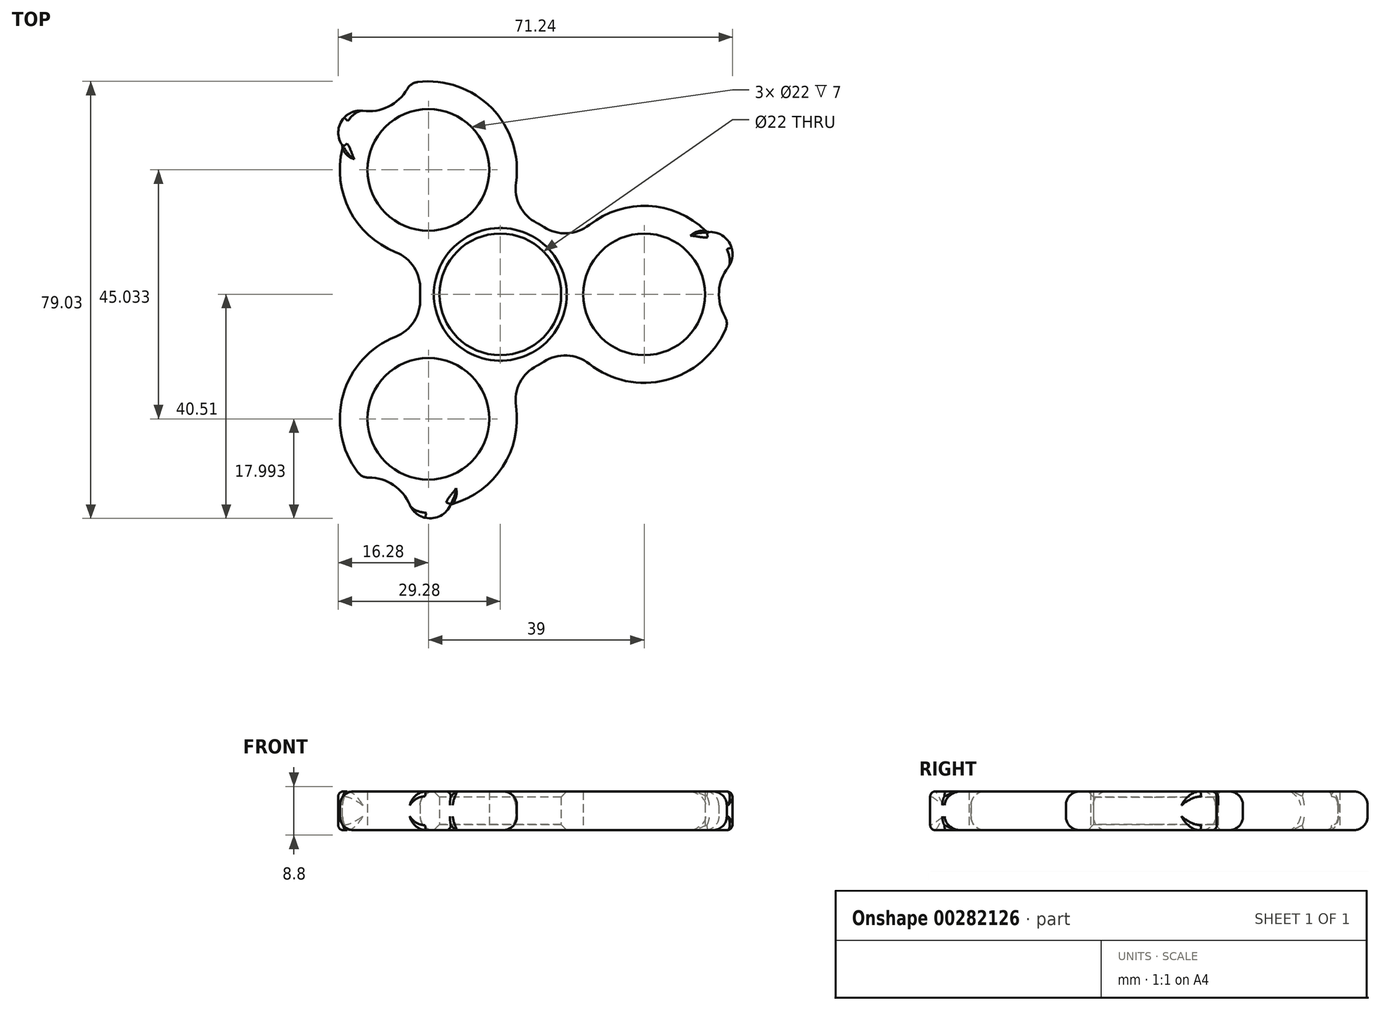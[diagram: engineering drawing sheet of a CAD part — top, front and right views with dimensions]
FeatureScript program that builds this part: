
annotation { "Feature Type Name" : "Feature", "Feature Type Description" : "" }
export const myFeature = defineFeature(function(context is Context, id is Id, definition is map)
    precondition{}
    {
        {
            var Q0;
            Q0=qCreatedBy(makeId("Top.planeOp"),FACE);
            var sketch = newSketch(context, id + "F0", { "sketchPlane" : qUnion([Q0])});
            skCircle(sketch, "E0", {"center": v(0, 0) * mm, "radius": 11 * mm});
            skCircle(sketch, "E1", {"center": v(0, 0) * mm, "radius": 14.5 * mm});
            skLineSegment(sketch, "E2", {"start": v(0, 0) * mm, "end": v(22, 0) * mm, "construction": true});
            skLineSegment(sketch, "E3", {"start": v(0, 0) * mm, "end": v(26, 0) * mm, "construction": true});
            skCircle(sketch, "E4", {"center": v(26, 0) * mm, "radius": 11 * mm});
            skCircle(sketch, "E5", {"center": v(26, 0) * mm, "radius": 16 * mm});
            skArc(sketch, "E6", {"start": v(17.92, 14.74) * mm, "mid": v(11.38, 11.05) * mm, "end": v(5.2, 15.34) * mm});
            skArc(sketch, "E7.MirrorCS", {"start": v(17.92, -14.74) * mm, "mid": v(11.38, -11.05) * mm, "end": v(5.2, -15.34) * mm});
            skLineSegment(sketch, "E8", {"start": v(39.86, 7.99) * mm, "end": v(62.74, 7.99) * mm, "construction": true});
            skLineSegment(sketch, "E9", {"start": v(39.86, -7.99) * mm, "end": v(63.47, -7.99) * mm, "construction": true});
            skArc(sketch, "E10", {"start": v(47.98, 7.99) * mm, "mid": v(39.5, 0) * mm, "end": v(47.98, -7.99) * mm});
            skLineSegment(sketch, "E11", {"start": v(47.5, 0) * mm, "end": v(61.75, 0) * mm, "construction": true});
            skArc(sketch, "E12", {"start": v(41.22, 4.95) * mm, "mid": v(41.38, 9.36) * mm, "end": v(37.4, 11.24) * mm});
            skArc(sketch, "E13.MirrorCS", {"start": v(41.22, -4.95) * mm, "mid": v(41.38, -9.36) * mm, "end": v(37.4, -11.24) * mm});
            skSolve(sketch);
        }
        {
            var Q0;
            Q0=makeQuery(id+"F0.imprint","IMPRINT",FACE,{"disambiguationData":[TD([[makeQuery(id+"F0.imprint","IMPRINT",EDGE,{"derivedFrom":sQuery(id+"F0.wireOp",EDGE,"E0")}),-1.0]])]});
            var Q1;
            {var subQ0=sQuery(id+"F0.wireOp",EDGE,"E5");var subQ1=sQuery(id+"F0.wireOp",EDGE,"E1");var subQ2=makeQuery(id+"F0.imprint","INTERSECT",VERTEX,{"disambiguationData":[OD(0.0)],"derivedFrom":[subQ1,subQ0]});Q1=makeQuery(id+"F0.imprint","IMPRINT",FACE,{"disambiguationData":[TD([[makeQuery(id+"F0.imprint","IMPRINT",EDGE,{"disambiguationData":[TD([[subQ2,1.0]])],"derivedFrom":subQ1}),1.0]])]});}
            var Q2;
            {var subQ2=sQuery(id+"F0.wireOp",EDGE,"E5");var subQ6=sQuery(id+"F0.wireOp",EDGE,"E0");var subQ7=makeQuery(id+"F0.imprint","INTERSECT",VERTEX,{"disambiguationData":[OD(0.0)],"derivedFrom":[subQ6,subQ2]});Q2=makeQuery(id+"F0.imprint","IMPRINT",FACE,{"disambiguationData":[TD([[makeQuery(id+"F0.imprint","IMPRINT",EDGE,{"disambiguationData":[TD([[subQ7,-1.0]])],"derivedFrom":subQ6}),-1.0]])]});}
            var Q3;
            Q3=makeQuery(id+"F0.imprint","IMPRINT",FACE,{"disambiguationData":[TD([[makeQuery(id+"F0.imprint","IMPRINT",EDGE,{"derivedFrom":sQuery(id+"F0.wireOp",EDGE,"E4")}),-1.0]])]});
            var Q4;
            {var subQ0=sQuery(id+"F0.wireOp",EDGE,"77vSXEcB-7QME-UigS-LLDl-sR1FWXDOiMO5");Q4=makeQuery(id+"F0.imprint","IMPRINT",FACE,{"disambiguationData":[TD([[makeQuery(id+"F0.imprint","IMPRINT",EDGE,{"derivedFrom":subQ0}),1.0]])]});}
            var Q5;
            {var subQ0=sQuery(id+"F0.wireOp",EDGE,"57d59b85-bc0c-4665-9c2c-a47e944732400.MirrorCS");Q5=makeQuery(id+"F0.imprint","IMPRINT",FACE,{"disambiguationData":[TD([[makeQuery(id+"F0.imprint","IMPRINT",EDGE,{"derivedFrom":subQ0}),-1.0]])]});}
            var Q6;
            {var subQ0=sQuery(id+"F0.wireOp",EDGE,"E12");Q6=makeQuery(id+"F0.imprint","IMPRINT",FACE,{"disambiguationData":[TD([[makeQuery(id+"F0.imprint","IMPRINT",EDGE,{"derivedFrom":subQ0}),1.0]])]});}
            var Q7;
            {var subQ0=sQuery(id+"F0.wireOp",EDGE,"E13.MirrorCS");Q7=makeQuery(id+"F0.imprint","IMPRINT",FACE,{"disambiguationData":[TD([[makeQuery(id+"F0.imprint","IMPRINT",EDGE,{"derivedFrom":subQ0}),-1.0]])]});}
            extrude(context, id + "F1", {"entities" : qUnion([Q0, Q1, Q2, Q3, Q4, Q5, Q6, Q7]), "endBound" : BoundingType.SYMMETRIC, "depth" : 7 * mm});
        }
        {
            var Q0;
            {var subQ0=sQuery(id+"F0.wireOp",EDGE,"E6");var subQ1=sQuery(id+"F0.wireOp",EDGE,"E1");var subQ2=makeQuery(id+"F0.imprint","INTERSECT",VERTEX,{"derivedFrom":[subQ1,subQ0]});Q0=makeQuery(id+"F0.imprint","IMPRINT",FACE,{"disambiguationData":[TD([[makeQuery(id+"F0.imprint","IMPRINT",EDGE,{"disambiguationData":[TD([[subQ2,1.0]])],"derivedFrom":subQ1}),-1.0]])]});}
            var Q1;
            Q1=makeQuery(id+"F0.imprint","IMPRINT",FACE,{"disambiguationData":[TD([[makeQuery(id+"F0.imprint","IMPRINT",EDGE,{"derivedFrom":sQuery(id+"F0.wireOp",EDGE,"E4")}),-1.0]])]});
            var Q2;
            {var subQ0=sQuery(id+"F0.wireOp",EDGE,"gSAZEsJJ-cn3l-cjJ6-9HDa-52uPBN5IA6vx");Q2=makeQuery(id+"F0.imprint","IMPRINT",FACE,{"disambiguationData":[TD([[makeQuery(id+"F0.imprint","IMPRINT",EDGE,{"derivedFrom":subQ0}),1.0]])]});}
            var Q3;
            {var subQ0=sQuery(id+"F0.wireOp",EDGE,"VPdpeA7V-GjOX-LRlJ-2Vj8-VplDRYYToLq0");Q3=makeQuery(id+"F0.imprint","IMPRINT",FACE,{"disambiguationData":[TD([[makeQuery(id+"F0.imprint","IMPRINT",EDGE,{"derivedFrom":subQ0}),1.0]])]});}
            var Q4;
            {var subQ0=sQuery(id+"F0.wireOp",EDGE,"f63044cd-322f-4f96-b824-94d15fe920c80.MirrorCS");Q4=makeQuery(id+"F0.imprint","IMPRINT",FACE,{"disambiguationData":[TD([[makeQuery(id+"F0.imprint","IMPRINT",EDGE,{"derivedFrom":subQ0}),-1.0]])]});}
            var Q5;
            {var subQ0=sQuery(id+"F0.wireOp",EDGE,"f037a777-31d1-4705-85f1-b677b52131420.MirrorCS");Q5=makeQuery(id+"F0.imprint","IMPRINT",FACE,{"disambiguationData":[TD([[makeQuery(id+"F0.imprint","IMPRINT",EDGE,{"derivedFrom":subQ0}),-1.0]])]});}
            var Q6;
            {var subQ0=sQuery(id+"F0.wireOp",EDGE,"a2668e3b-8a0b-417b-9202-db38daa61a800.MirrorCS");Q6=makeQuery(id+"F0.imprint","IMPRINT",FACE,{"disambiguationData":[TD([[makeQuery(id+"F0.imprint","IMPRINT",EDGE,{"derivedFrom":subQ0}),-1.0]])]});}
            var Q7;
            {var subQ0=sQuery(id+"F0.wireOp",EDGE,"diWcMJ20-Xh2n-FcUL-icb3-4419BL6dKp2H");Q7=makeQuery(id+"F0.imprint","IMPRINT",FACE,{"disambiguationData":[TD([[makeQuery(id+"F0.imprint","IMPRINT",EDGE,{"derivedFrom":subQ0}),1.0]])]});}
            var Q8;
            {var subQ0=sQuery(id+"F0.wireOp",EDGE,"E7.MirrorCS");var subQ1=sQuery(id+"F0.wireOp",EDGE,"E1");var subQ2=makeQuery(id+"F0.imprint","INTERSECT",VERTEX,{"derivedFrom":[subQ1,subQ0]});Q8=makeQuery(id+"F0.imprint","IMPRINT",FACE,{"disambiguationData":[TD([[makeQuery(id+"F0.imprint","IMPRINT",EDGE,{"disambiguationData":[TD([[subQ2,-1.0]])],"derivedFrom":subQ1}),-1.0]])]});}
            extrude(context, id + "F2", {"entities" : qUnion([Q0, Q1, Q2, Q3, Q4, Q5, Q6, Q7, Q8]), "operationType" : NewBodyOperationType.ADD, "endBound" : BoundingType.SYMMETRIC, "depth" : 7 * mm});
        }
        {
            var Q0;
            Q0=makeQuery(id+"F2.opExtrude","CAP_EDGE",EDGE,{"disambiguationData":[OSD([sQuery(id+"F0.wireOp",EDGE,"E6")])],"isStart":false});
            var Q1;
            Q1=makeQuery(id+"F2.opExtrude","CAP_EDGE",EDGE,{"disambiguationData":[OSD([sQuery(id+"F0.wireOp",EDGE,"gSAZEsJJ-cn3l-cjJ6-9HDa-52uPBN5IA6vx")])],"isStart":false});
            var Q2;
            Q2=makeQuery(id+"F2.opExtrude","CAP_EDGE",EDGE,{"disambiguationData":[OSD([sQuery(id+"F0.wireOp",EDGE,"VPdpeA7V-GjOX-LRlJ-2Vj8-VplDRYYToLq0")])],"isStart":false});
            var Q3;
            Q3=makeQuery(id+"F2.opExtrude","CAP_EDGE",EDGE,{"disambiguationData":[OSD([sQuery(id+"F0.wireOp",EDGE,"diWcMJ20-Xh2n-FcUL-icb3-4419BL6dKp2H")])],"isStart":false});
            var Q4;
            Q4=makeQuery(id+"F2.opExtrude","CAP_EDGE",EDGE,{"disambiguationData":[OSD([sQuery(id+"F0.wireOp",EDGE,"a2668e3b-8a0b-417b-9202-db38daa61a800.MirrorCS")])],"isStart":false});
            var Q5;
            Q5=makeQuery(id+"F2.opExtrude","CAP_EDGE",EDGE,{"disambiguationData":[OSD([sQuery(id+"F0.wireOp",EDGE,"f037a777-31d1-4705-85f1-b677b52131420.MirrorCS")])],"isStart":false});
            var Q6;
            Q6=makeQuery(id+"F2.opExtrude","CAP_EDGE",EDGE,{"disambiguationData":[OSD([sQuery(id+"F0.wireOp",EDGE,"f63044cd-322f-4f96-b824-94d15fe920c80.MirrorCS")])],"isStart":false});
            var Q7;
            Q7=makeQuery(id+"F2.opExtrude","CAP_EDGE",EDGE,{"disambiguationData":[OSD([sQuery(id+"F0.wireOp",EDGE,"E7.MirrorCS")])],"isStart":false});
            var Q8;
            Q8=makeQuery(id+"F2.opExtrude","CAP_EDGE",EDGE,{"disambiguationData":[OSD([sQuery(id+"F0.wireOp",EDGE,"E6")])],"isStart":true});
            var Q9;
            Q9=makeQuery(id+"F2.opExtrude","CAP_EDGE",EDGE,{"disambiguationData":[OSD([sQuery(id+"F0.wireOp",EDGE,"E7.MirrorCS")])],"isStart":true});
            var Q10;
            Q10=makeQuery(id+"F2.opExtrude","CAP_EDGE",EDGE,{"disambiguationData":[OSD([sQuery(id+"F0.wireOp",EDGE,"gSAZEsJJ-cn3l-cjJ6-9HDa-52uPBN5IA6vx")])],"isStart":true});
            var Q11;
            Q11=makeQuery(id+"F2.opExtrude","CAP_EDGE",EDGE,{"disambiguationData":[OSD([sQuery(id+"F0.wireOp",EDGE,"VPdpeA7V-GjOX-LRlJ-2Vj8-VplDRYYToLq0")])],"isStart":true});
            var Q12;
            Q12=makeQuery(id+"F2.opExtrude","CAP_EDGE",EDGE,{"disambiguationData":[OSD([sQuery(id+"F0.wireOp",EDGE,"diWcMJ20-Xh2n-FcUL-icb3-4419BL6dKp2H")])],"isStart":true});
            var Q13;
            Q13=makeQuery(id+"F2.opExtrude","CAP_EDGE",EDGE,{"disambiguationData":[OSD([sQuery(id+"F0.wireOp",EDGE,"a2668e3b-8a0b-417b-9202-db38daa61a800.MirrorCS")])],"isStart":true});
            var Q14;
            Q14=makeQuery(id+"F2.opExtrude","CAP_EDGE",EDGE,{"disambiguationData":[OSD([sQuery(id+"F0.wireOp",EDGE,"f037a777-31d1-4705-85f1-b677b52131420.MirrorCS")])],"isStart":true});
            var Q15;
            Q15=makeQuery(id+"F2.opExtrude","CAP_EDGE",EDGE,{"disambiguationData":[OSD([sQuery(id+"F0.wireOp",EDGE,"f63044cd-322f-4f96-b824-94d15fe920c80.MirrorCS")])],"isStart":true});
            var Q16;
            Q16=makeQuery(id+"F1.opExtrude","SWEPT_FACE",FACE,{"disambiguationData":[OSD([sQuery(id+"F0.wireOp",EDGE,"E10")])]});
            fillet(context, id + "F3", {"entities" : qUnion([Q0, Q1, Q2, Q3, Q4, Q5, Q6, Q7, Q8, Q9, Q10, Q11, Q12, Q13, Q14, Q15, Q16]), "radius" : 2.5 * mm, "tangentPropagation" : true, "allowEdgeOverflow" : false});
        }
        {
            var Q0;
            Q0=makeQuery(id+"F1.opExtrude","SWEPT_FACE",FACE,{"disambiguationData":[OSD([sQuery(id+"F0.wireOp",EDGE,"E12")])]});
            var Q1;
            Q1=makeQuery(id+"F1.opExtrude","SWEPT_FACE",FACE,{"disambiguationData":[OSD([sQuery(id+"F0.wireOp",EDGE,"E13.MirrorCS")])]});
            fillet(context, id + "F4", {"entities" : qUnion([Q0, Q1]), "radius" : 0.9 * mm, "tangentPropagation" : true, "allowEdgeOverflow" : false});
        }
        {
            var Q0;
            Q0=makeQuery(id+"F1.opExtrude","SWEPT_FACE",FACE,{"disambiguationData":[OSD([sQuery(id+"F0.wireOp",EDGE,"E0")])]});
            var Q1;
            Q1=makeQuery(id+"F2.opExtrude","SWEPT_FACE",FACE,{"disambiguationData":[OSD([sQuery(id+"F0.wireOp",EDGE,"E4")])]});
            chamfer(context, id + "F5", {"entities" : qUnion([Q0, Q1]), "width" : 1 * mm, "tangentPropagation" : true});
        }
        {
            var Q0;
            Q0=makeQuery(id+"F1.opExtrude","SWEPT_BODY",BODY,{"disambiguationData":[OSD([sQuery(id+"F0.wireOp",EDGE,"E0"),sQuery(id+"F0.wireOp",EDGE,"E1"),sQuery(id+"F0.wireOp",EDGE,"E4"),sQuery(id+"F0.wireOp",EDGE,"E6"),sQuery(id+"F0.wireOp",EDGE,"E7.MirrorCS"),sQuery(id+"F0.wireOp",EDGE,"gSAZEsJJ-cn3l-cjJ6-9HDa-52uPBN5IA6vx"),sQuery(id+"F0.wireOp",EDGE,"VPdpeA7V-GjOX-LRlJ-2Vj8-VplDRYYToLq0"),sQuery(id+"F0.wireOp",EDGE,"diWcMJ20-Xh2n-FcUL-icb3-4419BL6dKp2H"),sQuery(id+"F0.wireOp",EDGE,"f63044cd-322f-4f96-b824-94d15fe920c80.MirrorCS"),sQuery(id+"F0.wireOp",EDGE,"f037a777-31d1-4705-85f1-b677b52131420.MirrorCS"),sQuery(id+"F0.wireOp",EDGE,"a2668e3b-8a0b-417b-9202-db38daa61a800.MirrorCS")])]});
            var Q1;
            Q1=makeQuery(id+"F1.opExtrude","SWEPT_FACE",FACE,{"disambiguationData":[OSD([sQuery(id+"F0.wireOp",EDGE,"E0")])]});
            circularPattern(context, id + "F6", {"operationType" : NewBodyOperationType.ADD, "entities" : qUnion([Q0]), "axis" : qUnion([Q1]), "angle" : 360 * degree, "instanceCount" : 3, "equalSpace" : true});
        }
    });
